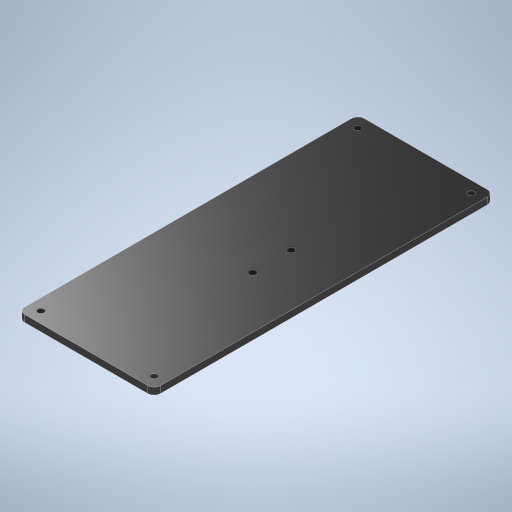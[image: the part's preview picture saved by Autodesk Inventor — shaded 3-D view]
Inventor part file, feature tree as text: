
AUTODESK INVENTOR PART (.ipt)
format: ipt  version: 2023 (Build 270158000, 158)  size: 270,336 bytes
history: native  units: in
note: dims shown in document units (in); Inventor stores cm internally (conversion verified against a paired STEP export)
features: fillet x4, extrude x1, sketch x1
ambient origin geometry x8: Origin, YZ Plane, XZ Plane, XY Plane, X Axis, Y Axis, Z Axis, Center Point
bodies: Solid1 (feature_tree)
feature tree (6):
  extrude  "Extrusion1"  Depth=0.1181in TaperAngle=0.0deg
  fillet  "Fillet1"  Radius=0.1102in
  fillet  "Fillet2"  Radius=0.1102in
  fillet  "Fillet3"  Radius=0.1102in
  fillet  "Fillet4"  Radius=0.1102in
  sketch  "Sketch1"  dims[d0=2.3622in d1=5.9055in d2=0.1969in d3=0.1969in d4=0.1969in d5=0.1969in d6=0.1969in d8=0.1969in d10=0.1102in d11=0.1102in d12=0.7492in d13=0.8681in d14=0.0984in d15=0.0984in d16=0.0984in d17=0.0984in d18=0.1181in d19=0.1181in d20=0.0394in d21=0.1575in d41=0.1181in d42=0.0in d43=0.1102in d44=0.1102in d45=0.1102in d46=0.1102in]
